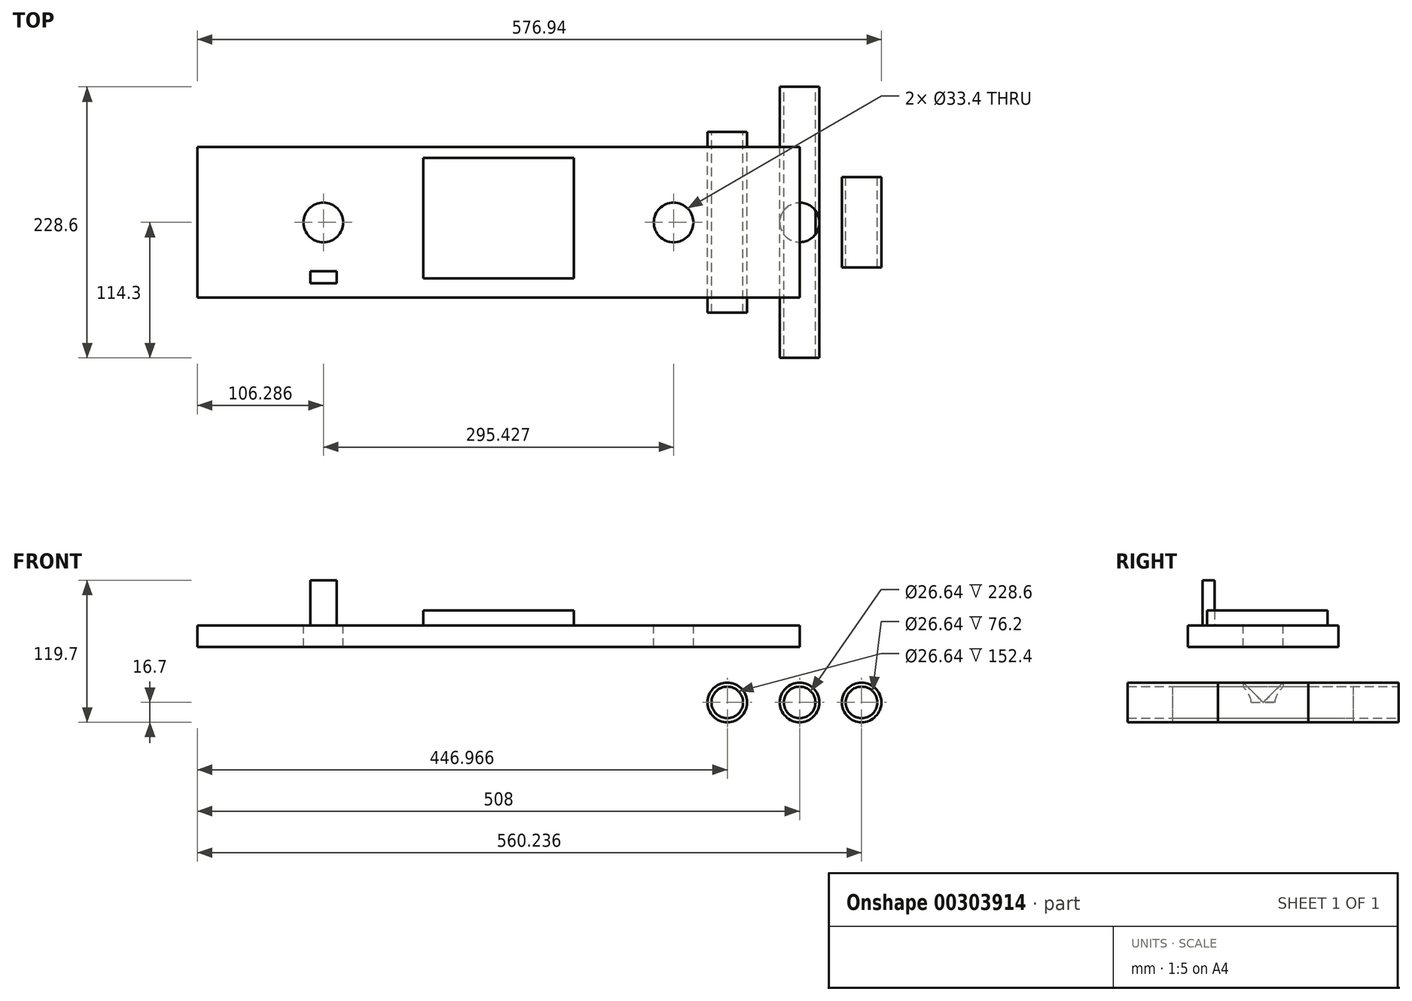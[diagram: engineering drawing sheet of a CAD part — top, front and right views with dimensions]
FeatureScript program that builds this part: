
annotation { "Feature Type Name" : "Feature", "Feature Type Description" : "" }
export const myFeature = defineFeature(function(context is Context, id is Id, definition is map)
    precondition{}
    {
        {
            var Q0;
            Q0=qCreatedBy(makeId("Front.planeOp"),FACE);
            var sketch = newSketch(context, id + "F0", { "sketchPlane" : qUnion([Q0])});
            skCircle(sketch, "E0", {"center": v(0, 0) * mm, "radius": 16.7 * mm});
            skCircle(sketch, "E1", {"center": v(-61.03, 0) * mm, "radius": 16.7 * mm});
            skCircle(sketch, "E2", {"center": v(52.24, 0) * mm, "radius": 16.7 * mm});
            skCircle(sketch, "E3", {"center": v(-61.03, 0) * mm, "radius": 13.32 * mm});
            skCircle(sketch, "E4", {"center": v(0, 0) * mm, "radius": 13.32 * mm});
            skCircle(sketch, "E5", {"center": v(52.24, 0) * mm, "radius": 13.32 * mm});
            skSolve(sketch);
        }
        {
            var Q0;
            Q0=makeQuery(id+"F0.imprint","IMPRINT",FACE,{"disambiguationData":[TD([[makeQuery(id+"F0.imprint","IMPRINT",EDGE,{"derivedFrom":sQuery(id+"F0.wireOp",EDGE,"E1")}),1.0]])]});
            extrude(context, id + "F1", {"entities" : qUnion([Q0]), "endBound" : BoundingType.SYMMETRIC, "depth" : 152.4 * mm});
        }
        {
            var Q0;
            Q0=makeQuery(id+"F0.imprint","IMPRINT",FACE,{"disambiguationData":[TD([[makeQuery(id+"F0.imprint","IMPRINT",EDGE,{"derivedFrom":sQuery(id+"F0.wireOp",EDGE,"E0")}),1.0]])]});
            extrude(context, id + "F2", {"entities" : qUnion([Q0]), "endBound" : BoundingType.SYMMETRIC, "depth" : 228.6 * mm});
        }
        {
            var Q0;
            Q0=makeQuery(id+"F0.imprint","IMPRINT",FACE,{"disambiguationData":[TD([[makeQuery(id+"F0.imprint","IMPRINT",EDGE,{"derivedFrom":sQuery(id+"F0.wireOp",EDGE,"E2")}),1.0]])]});
            extrude(context, id + "F3", {"entities" : qUnion([Q0]), "endBound" : BoundingType.SYMMETRIC, "depth" : 76.2 * mm});
        }
        {
            var Q0;
            Q0=qCreatedBy(makeId("Front.planeOp"),FACE);
            var sketch = newSketch(context, id + "F4", { "sketchPlane" : qUnion([Q0])});
            skLineSegment(sketch, "E6", {"start": v(-508, 64.9) * mm, "end": v(-508, 46.64) * mm});
            skLineSegment(sketch, "E7", {"start": v(-508, 46.64) * mm, "end": v(0, 46.64) * mm});
            skLineSegment(sketch, "E8", {"start": v(0, 46.64) * mm, "end": v(0, 64.9) * mm});
            skLineSegment(sketch, "E9", {"start": v(0, 64.9) * mm, "end": v(-508, 64.9) * mm});
            skSolve(sketch);
        }
        {
            var Q0;
            Q0=makeQuery(id+"F4.imprint","IMPRINT",FACE,{"disambiguationData":[TD([[makeQuery(id+"F4.imprint","IMPRINT",EDGE,{"derivedFrom":sQuery(id+"F4.wireOp",EDGE,"E6")}),1.0]])]});
            extrude(context, id + "F5", {"entities" : qUnion([Q0]), "endBound" : BoundingType.SYMMETRIC, "depth" : 127 * mm});
        }
        {
            var Q0;
            Q0=qCreatedBy(makeId("Top.planeOp"),FACE);
            var sketch = newSketch(context, id + "F6", { "sketchPlane" : qUnion([Q0])});
            skLineSegment(sketch, "E10.bottom", {"start": v(-16.7, -12.7) * mm, "end": v(16.7, -12.7) * mm});
            skLineSegment(sketch, "E10.top", {"start": v(-16.7, 12.7) * mm, "end": v(16.7, 12.7) * mm});
            skLineSegment(sketch, "E10.left", {"start": v(-16.7, -12.7) * mm, "end": v(-16.7, 12.7) * mm});
            skLineSegment(sketch, "E10.right", {"start": v(16.7, -12.7) * mm, "end": v(16.7, 12.7) * mm});
            skLineSegment(sketch, "E11", {"start": v(-16.7, 0) * mm, "end": v(-16.7, -12.7) * mm});
            skCircle(sketch, "E12", {"center": v(0, 0) * mm, "radius": 16.7 * mm});
            skSolve(sketch);
        }
        {
            var Q0;
            {var subQ0=sQuery(id+"F6.wireOp",EDGE,"E12");var subQ1=sQuery(id+"F6.wireOp",EDGE,"E10.top");var subQ2=makeQuery(id+"F6.imprint","INTERSECT",VERTEX,{"disambiguationData":[OD(0.0)],"derivedFrom":[subQ1,subQ0]});Q0=makeQuery(id+"F6.imprint","IMPRINT",FACE,{"disambiguationData":[TD([[makeQuery(id+"F6.imprint","IMPRINT",EDGE,{"disambiguationData":[TD([[subQ2,-1.0]])],"derivedFrom":subQ1}),1.0]])]});}
            var Q1;
            {var subQ0=sQuery(id+"F6.wireOp",EDGE,"E12");var subQ4=sQuery(id+"F6.wireOp",EDGE,"E10.bottom");var subQ5=makeQuery(id+"F6.imprint","INTERSECT",VERTEX,{"disambiguationData":[OD(0.0)],"derivedFrom":[subQ4,subQ0]});Q1=makeQuery(id+"F6.imprint","IMPRINT",FACE,{"disambiguationData":[TD([[makeQuery(id+"F6.imprint","IMPRINT",EDGE,{"disambiguationData":[TD([[subQ5,-1.0]])],"derivedFrom":subQ4}),1.0]])]});}
            var Q2;
            {var subQ0=sQuery(id+"F6.wireOp",EDGE,"E12");var subQ1=sQuery(id+"F6.wireOp",EDGE,"E10.bottom");var subQ2=makeQuery(id+"F6.imprint","INTERSECT",VERTEX,{"disambiguationData":[OD(0.0)],"derivedFrom":[subQ1,subQ0]});Q2=makeQuery(id+"F6.imprint","IMPRINT",FACE,{"disambiguationData":[TD([[makeQuery(id+"F6.imprint","IMPRINT",EDGE,{"disambiguationData":[TD([[subQ2,-1.0]])],"derivedFrom":subQ1}),-1.0]])]});}
            var Q3;
            Q3=sQuery(id+"F6.wireOp",EDGE,"E12");
            extrude(context, id + "F7", {"entities" : qUnion([Q0, Q1, Q2]), "operationType" : NewBodyOperationType.REMOVE, "surfaceEntities" : qUnion([Q3]), "depth" : 25.4 * mm});
        }
        {
            var Q0;
            Q0=makeQuery(id+"F5.opExtrude","SWEPT_FACE",FACE,{"disambiguationData":[OSD([sQuery(id+"F4.wireOp",EDGE,"E9")])]});
            var sketch = newSketch(context, id + "F8", { "sketchPlane" : qUnion([Q0])});
            skLineSegment(sketch, "E13", {"start": v(-385.01, 0) * mm, "end": v(-122.99, 0) * mm});
            skLineSegment(sketch, "E14", {"start": v(-122.99, 0) * mm, "end": v(0, 0) * mm, "construction": true});
            skLineSegment(sketch, "E15", {"start": v(-385.01, 0) * mm, "end": v(-508, 0) * mm, "construction": true});
            skLineSegment(sketch, "E16", {"start": v(-254, 93.15) * mm, "end": v(-254, -107.82) * mm, "construction": true});
            skPoint(sketch, "E16.startSnap0", {"position": v(-254, 63.5) * mm});
            skPoint(sketch, "E16.endSnap0", {"position": v(-254, -63.5) * mm});
            skLineSegment(sketch, "E17", {"start": v(-385.01, 0) * mm, "end": v(-385.01, 25.4) * mm});
            skLineSegment(sketch, "E18", {"start": v(-385.01, 0) * mm, "end": v(-385.01, -25.4) * mm});
            skLineSegment(sketch, "E19.bottom", {"start": v(-385.01, -25.4) * mm, "end": v(-418.41, -25.4) * mm});
            skLineSegment(sketch, "E19.top", {"start": v(-385.01, -31.75) * mm, "end": v(-418.41, -31.75) * mm});
            skLineSegment(sketch, "E19.left", {"start": v(-385.01, -25.4) * mm, "end": v(-385.01, -31.75) * mm});
            skLineSegment(sketch, "E19.right", {"start": v(-418.41, -25.4) * mm, "end": v(-418.41, -31.75) * mm});
            skLineSegment(sketch, "E20.bottom", {"start": v(-385.01, 25.4) * mm, "end": v(-418.41, 25.4) * mm});
            skLineSegment(sketch, "E20.top", {"start": v(-385.01, 31.75) * mm, "end": v(-418.41, 31.75) * mm});
            skLineSegment(sketch, "E20.left", {"start": v(-385.01, 25.4) * mm, "end": v(-385.01, 31.75) * mm});
            skLineSegment(sketch, "E20.right", {"start": v(-418.41, 25.4) * mm, "end": v(-418.41, 31.75) * mm});
            skLineSegment(sketch, "E21", {"start": v(-122.99, 0) * mm, "end": v(-122.99, 25.4) * mm, "construction": true});
            skLineSegment(sketch, "E22", {"start": v(-122.99, 0) * mm, "end": v(-122.99, -25.4) * mm, "construction": true});
            skLineSegment(sketch, "E23", {"start": v(-122.99, 25.4) * mm, "end": v(-89.59, 25.4) * mm});
            skLineSegment(sketch, "E24", {"start": v(-89.59, 25.4) * mm, "end": v(-89.59, 31.75) * mm});
            skLineSegment(sketch, "E25", {"start": v(-89.59, 31.75) * mm, "end": v(-122.99, 31.75) * mm});
            skLineSegment(sketch, "E26", {"start": v(-122.99, 31.75) * mm, "end": v(-122.99, 25.4) * mm});
            skLineSegment(sketch, "E27", {"start": v(-122.99, -25.4) * mm, "end": v(-89.59, -25.4) * mm});
            skLineSegment(sketch, "E28", {"start": v(-89.59, -25.4) * mm, "end": v(-89.59, -31.75) * mm});
            skLineSegment(sketch, "E29", {"start": v(-89.59, -31.75) * mm, "end": v(-122.99, -31.75) * mm});
            skLineSegment(sketch, "E30", {"start": v(-122.99, -31.75) * mm, "end": v(-122.99, -25.4) * mm});
            skCircle(sketch, "E31", {"center": v(-401.71, 0) * mm, "radius": 16.7 * mm});
            skPoint(sketch, "E31.centerSnap0", {"position": v(-401.71, 25.4) * mm});
            skCircle(sketch, "E32", {"center": v(-106.29, 0) * mm, "radius": 16.7 * mm});
            skPoint(sketch, "E32.centerSnap0", {"position": v(-106.29, 25.4) * mm});
            skSolve(sketch);
        }
        {
            var Q0;
            Q0=makeQuery(id+"F8.imprint","IMPRINT",FACE,{"disambiguationData":[TD([[makeQuery(id+"F8.imprint","IMPRINT",EDGE,{"derivedFrom":sQuery(id+"F8.wireOp",EDGE,"E32")}),1.0]])]});
            var Q1;
            Q1=makeQuery(id+"F8.imprint","IMPRINT",FACE,{"disambiguationData":[TD([[makeQuery(id+"F8.imprint","IMPRINT",EDGE,{"derivedFrom":sQuery(id+"F8.wireOp",EDGE,"E31")}),1.0]])]});
            extrude(context, id + "F9", {"entities" : qUnion([Q0, Q1]), "operationType" : NewBodyOperationType.REMOVE, "oppositeDirection" : true, "depth" : 25.4 * mm});
        }
        {
            var Q0;
            Q0=makeQuery(id+"F5.opExtrude","SWEPT_FACE",FACE,{"disambiguationData":[OSD([sQuery(id+"F4.wireOp",EDGE,"E9")])]});
            var sketch = newSketch(context, id + "F10", { "sketchPlane" : qUnion([Q0])});
            skLineSegment(sketch, "E33.bottom", {"start": v(-317.5, -47.23) * mm, "end": v(-190.5, -47.23) * mm});
            skLineSegment(sketch, "E33.top", {"start": v(-317.5, 54.37) * mm, "end": v(-190.5, 54.37) * mm});
            skLineSegment(sketch, "E33.left", {"start": v(-317.5, -47.23) * mm, "end": v(-317.5, 54.37) * mm});
            skLineSegment(sketch, "E33.right", {"start": v(-190.5, -47.23) * mm, "end": v(-190.5, 54.37) * mm});
            skPoint(sketch, "E34", {"position": v(-122.99, 0) * mm});
            skPoint(sketch, "E35", {"position": v(-385.01, 0) * mm});
            skLineSegment(sketch, "E36.bottom", {"start": v(-412.83, -41.07) * mm, "end": v(-390.6, -41.07) * mm});
            skLineSegment(sketch, "E36.top", {"start": v(-412.83, -51.23) * mm, "end": v(-390.6, -51.23) * mm});
            skLineSegment(sketch, "E36.left", {"start": v(-412.83, -41.07) * mm, "end": v(-412.83, -51.23) * mm});
            skLineSegment(sketch, "E36.right", {"start": v(-390.6, -41.07) * mm, "end": v(-390.6, -51.23) * mm});
            skPoint(sketch, "E37", {"position": v(-418.41, 0) * mm});
            skLineSegment(sketch, "E38", {"start": v(-401.71, 0) * mm, "end": v(-401.71, -59.3) * mm, "construction": true});
            skSolve(sketch);
        }
        {
            var Q0;
            Q0=makeQuery(id+"F10.imprint","IMPRINT",FACE,{"disambiguationData":[TD([[makeQuery(id+"F10.imprint","IMPRINT",EDGE,{"derivedFrom":sQuery(id+"F10.wireOp",EDGE,"E33.bottom")}),1.0]])]});
            extrude(context, id + "F11", {"entities" : qUnion([Q0]), "operationType" : NewBodyOperationType.ADD, "depth" : 12.7 * mm});
        }
        {
            var Q0;
            Q0=makeQuery(id+"F10.imprint","IMPRINT",FACE,{"disambiguationData":[TD([[makeQuery(id+"F10.imprint","IMPRINT",EDGE,{"derivedFrom":sQuery(id+"F10.wireOp",EDGE,"E36.bottom")}),-1.0]])]});
            extrude(context, id + "F12", {"entities" : qUnion([Q0]), "operationType" : NewBodyOperationType.ADD, "depth" : 38.1 * mm});
        }
    });
